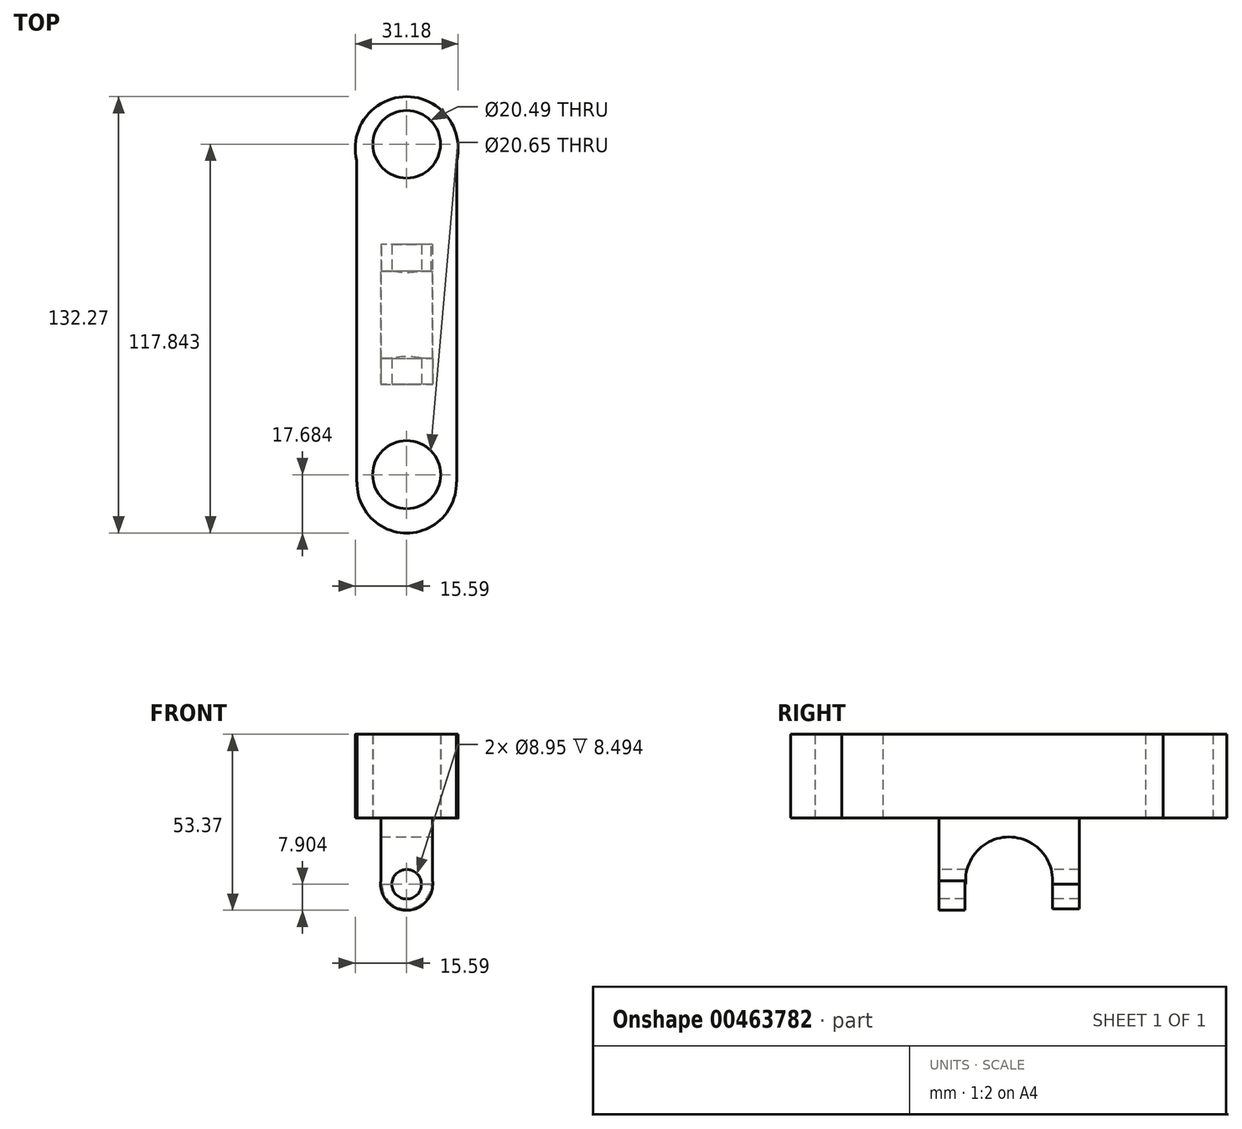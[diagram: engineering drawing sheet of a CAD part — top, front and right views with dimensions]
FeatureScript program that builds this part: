
annotation { "Feature Type Name" : "Feature", "Feature Type Description" : "" }
export const myFeature = defineFeature(function(context is Context, id is Id, definition is map)
    precondition{}
    {
        {
            var Q0;
            Q0=qCreatedBy(makeId("Top.planeOp"),FACE);
            var sketch = newSketch(context, id + "F0", { "sketchPlane" : qUnion([Q0])});
            skLineSegment(sketch, "E0.bottom", {"start": v(15.14, 50.74) * mm, "end": v(-15.14, 50.74) * mm});
            skLineSegment(sketch, "E0.top", {"start": v(15.14, -50.74) * mm, "end": v(-15.14, -50.74) * mm});
            skLineSegment(sketch, "E0.left", {"start": v(15.14, 50.74) * mm, "end": v(15.14, -50.74) * mm});
            skLineSegment(sketch, "E0.right", {"start": v(-15.14, 50.74) * mm, "end": v(-15.14, -50.74) * mm});
            skPoint(sketch, "E0.middle", {"position": v(0, 0) * mm});
            skSolve(sketch);
        }
        {
            var Q0;
            Q0=qCreatedBy(makeId("Top.planeOp"),FACE);
            var sketch = newSketch(context, id + "F1", { "sketchPlane" : qUnion([Q0])});
            skCircle(sketch, "E1", {"center": v(0, 50.42) * mm, "radius": 15.6 * mm});
            skSolve(sketch);
        }
        {
            var Q0;
            Q0=qCreatedBy(makeId("Top.planeOp"),FACE);
            var sketch = newSketch(context, id + "F2", { "sketchPlane" : qUnion([Q0])});
            skCircle(sketch, "E2", {"center": v(0, -51.2) * mm, "radius": 15.05 * mm});
            skSolve(sketch);
        }
        {
            var Q0;
            Q0=makeQuery(id+"F0.imprint","IMPRINT",FACE,{"disambiguationData":[TD([[makeQuery(id+"F0.imprint","IMPRINT",EDGE,{"derivedFrom":sQuery(id+"F0.wireOp",EDGE,"E0.bottom")}),1.0]])]});
            extrude(context, id + "F3", {"entities" : qUnion([Q0]), "depth" : 25.4 * mm});
        }
        {
            var Q0;
            Q0=makeQuery(id+"F2.imprint","IMPRINT",FACE,{"disambiguationData":[TD([[makeQuery(id+"F2.imprint","IMPRINT",EDGE,{"derivedFrom":sQuery(id+"F2.wireOp",EDGE,"E2")}),1.0]])]});
            extrude(context, id + "F4", {"entities" : qUnion([Q0]), "operationType" : NewBodyOperationType.ADD, "depth" : 25.4 * mm});
        }
        {
            var Q0;
            Q0=makeQuery(id+"F1.imprint","IMPRINT",FACE,{"disambiguationData":[TD([[makeQuery(id+"F1.imprint","IMPRINT",EDGE,{"derivedFrom":sQuery(id+"F1.wireOp",EDGE,"E1")}),1.0]])]});
            extrude(context, id + "F5", {"entities" : qUnion([Q0]), "operationType" : NewBodyOperationType.ADD, "depth" : 25.4 * mm});
        }
        {
            var Q0;
            Q0=qCreatedBy(makeId("Top.planeOp"),FACE);
            var sketch = newSketch(context, id + "F6", { "sketchPlane" : qUnion([Q0])});
            skCircle(sketch, "E3", {"center": v(0, 51.6) * mm, "radius": 10.24 * mm});
            skSolve(sketch);
        }
        {
            var Q0;
            Q0=makeQuery(id+"F6.imprint","IMPRINT",FACE,{"disambiguationData":[TD([[makeQuery(id+"F6.imprint","IMPRINT",EDGE,{"derivedFrom":sQuery(id+"F6.wireOp",EDGE,"E3")}),1.0]])]});
            extrude(context, id + "F7", {"entities" : qUnion([Q0]), "operationType" : NewBodyOperationType.REMOVE, "depth" : 49.02 * mm});
        }
        {
            var Q0;
            Q0=qCreatedBy(makeId("Top.planeOp"),FACE);
            var sketch = newSketch(context, id + "F8", { "sketchPlane" : qUnion([Q0])});
            skCircle(sketch, "E4", {"center": v(0, -48.57) * mm, "radius": 10.33 * mm});
            skSolve(sketch);
        }
        {
            var Q0;
            Q0=makeQuery(id+"F8.imprint","IMPRINT",FACE,{"disambiguationData":[TD([[makeQuery(id+"F8.imprint","IMPRINT",EDGE,{"derivedFrom":sQuery(id+"F8.wireOp",EDGE,"E4")}),1.0]])]});
            extrude(context, id + "F9", {"entities" : qUnion([Q0]), "operationType" : NewBodyOperationType.REMOVE, "depth" : 31.75 * mm});
        }
        {
            var Q0;
            Q0=qCreatedBy(makeId("Top.planeOp"),FACE);
            var sketch = newSketch(context, id + "F10", { "sketchPlane" : qUnion([Q0])});
            skLineSegment(sketch, "E5.bottom", {"start": v(7.83, 21.24) * mm, "end": v(-7.83, 21.24) * mm});
            skLineSegment(sketch, "E5.top", {"start": v(7.83, -21.24) * mm, "end": v(-7.83, -21.24) * mm});
            skLineSegment(sketch, "E5.left", {"start": v(7.83, 21.24) * mm, "end": v(7.83, -21.24) * mm});
            skLineSegment(sketch, "E5.right", {"start": v(-7.83, 21.24) * mm, "end": v(-7.83, -21.24) * mm});
            skPoint(sketch, "E5.middle", {"position": v(0, 0) * mm});
            skSolve(sketch);
        }
        {
            var Q0;
            Q0=makeQuery(id+"F10.imprint","IMPRINT",FACE,{"disambiguationData":[TD([[makeQuery(id+"F10.imprint","IMPRINT",EDGE,{"derivedFrom":sQuery(id+"F10.wireOp",EDGE,"E5.bottom")}),1.0]])]});
            extrude(context, id + "F11", {"entities" : qUnion([Q0]), "operationType" : NewBodyOperationType.ADD, "oppositeDirection" : true, "depth" : 20.07 * mm});
        }
        {
            var Q0;
            Q0=qCreatedBy(makeId("Right.planeOp"),FACE);
            var sketch = newSketch(context, id + "F12", { "sketchPlane" : qUnion([Q0])});
            skCircle(sketch, "E6", {"center": v(0, -18.92) * mm, "radius": 13.18 * mm});
            skSolve(sketch);
        }
        {
            var Q0;
            Q0=makeQuery(id+"F12.imprint","IMPRINT",FACE,{"disambiguationData":[TD([[makeQuery(id+"F12.imprint","IMPRINT",EDGE,{"derivedFrom":sQuery(id+"F12.wireOp",EDGE,"E6")}),1.0]])]});
            extrude(context, id + "F13", {"entities" : qUnion([Q0]), "operationType" : NewBodyOperationType.REMOVE, "oppositeDirection" : true, "depth" : 25.4 * mm});
        }
        {
            var Q0;
            Q0=makeQuery(id+"F13.boolean.opBoolean","COPY",FACE,{"derivedFrom":makeQuery(id+"F13.opExtrude","CAP_FACE",FACE,{"disambiguationData":[OSD([sQuery(id+"F12.wireOp",EDGE,"E6")])],"isStart":true})});
            extrude(context, id + "F14", {"entities" : qUnion([Q0]), "operationType" : NewBodyOperationType.REMOVE, "oppositeDirection" : true, "depth" : 25.4 * mm});
        }
        {
            var Q0;
            Q0=makeQuery(id+"F11.opExtrude","SWEPT_FACE",FACE,{"disambiguationData":[OSD([sQuery(id+"F10.wireOp",EDGE,"E5.bottom")])]});
            var sketch = newSketch(context, id + "F15", { "sketchPlane" : qUnion([Q0])});
            skCircle(sketch, "E7", {"center": v(0, -20.07) * mm, "radius": 7.5 * mm});
            skSolve(sketch);
        }
        {
            var Q0;
            {var subQ0=sQuery(id+"F15.wireOp",EDGE,"E7");var subQ1=makeQuery(id+"F11.opExtrude","CAP_EDGE",EDGE,{"disambiguationData":[OSD([sQuery(id+"F10.wireOp",EDGE,"E5.bottom")])],"isStart":false});var subQ2=makeQuery(id+"F15.imprint","INTERSECT",VERTEX,{"disambiguationData":[OD(0.0)],"derivedFrom":[subQ1,subQ0]});Q0=makeQuery(id+"F15.imprint","IMPRINT",FACE,{"disambiguationData":[TD([[makeQuery(id+"F15.imprint","IMPRINT",EDGE,{"disambiguationData":[TD([[subQ2,-1.0]])],"derivedFrom":subQ0}),1.0]])]});}
            extrude(context, id + "F16", {"entities" : qUnion([Q0]), "operationType" : NewBodyOperationType.ADD, "oppositeDirection" : true, "depth" : 8.13 * mm});
        }
        {
            var Q0;
            Q0=makeQuery(id+"F11.opExtrude","SWEPT_FACE",FACE,{"disambiguationData":[OSD([sQuery(id+"F10.wireOp",EDGE,"E5.top")])]});
            var sketch = newSketch(context, id + "F17", { "sketchPlane" : qUnion([Q0])});
            skCircle(sketch, "E8", {"center": v(0, -20.07) * mm, "radius": 7.9 * mm});
            skSolve(sketch);
        }
        {
            var Q0;
            {var subQ1=sQuery(id+"F10.wireOp",EDGE,"E5.top");var subQ6=makeQuery(id+"F11.opExtrude","CAP_EDGE",EDGE,{"disambiguationData":[OSD([subQ1])],"isStart":false});Q0=makeQuery(id+"F17.imprint","IMPRINT",FACE,{"disambiguationData":[TD([[makeQuery(id+"F17.imprint","IMPRINT",EDGE,{"derivedFrom":subQ6}),1.0]])]});}
            extrude(context, id + "F18", {"entities" : qUnion([Q0]), "operationType" : NewBodyOperationType.ADD, "oppositeDirection" : true, "depth" : 7.87 * mm});
        }
        {
            var Q0;
            {var subQ0=sQuery(id+"F10.wireOp",EDGE,"E5.top");Q0=makeQuery(id+"F18.boolean.opBoolean","MERGE",FACE,{"derivedFrom":[makeQuery(id+"F11.opExtrude","SWEPT_FACE",FACE,{"disambiguationData":[OSD([subQ0])]}),makeQuery(id+"F18.opExtrude","CAP_FACE",FACE,{"disambiguationData":[OSD([subQ0,sQuery(id+"F10.wireOp",EDGE,"E5.left"),sQuery(id+"F10.wireOp",EDGE,"E5.right"),sQuery(id+"F17.wireOp",EDGE,"E8")])],"isStart":true})]});}
            var sketch = newSketch(context, id + "F19", { "sketchPlane" : qUnion([Q0])});
            skCircle(sketch, "E9", {"center": v(0, -20.07) * mm, "radius": 4.48 * mm});
            skSolve(sketch);
        }
        {
            var Q0;
            Q0=makeQuery(id+"F19.imprint","IMPRINT",FACE,{"disambiguationData":[TD([[makeQuery(id+"F19.imprint","IMPRINT",EDGE,{"derivedFrom":sQuery(id+"F19.wireOp",EDGE,"E9")}),1.0]])]});
            extrude(context, id + "F20", {"entities" : qUnion([Q0]), "operationType" : NewBodyOperationType.REMOVE, "oppositeDirection" : true, "depth" : 55.12 * mm});
        }
    });
